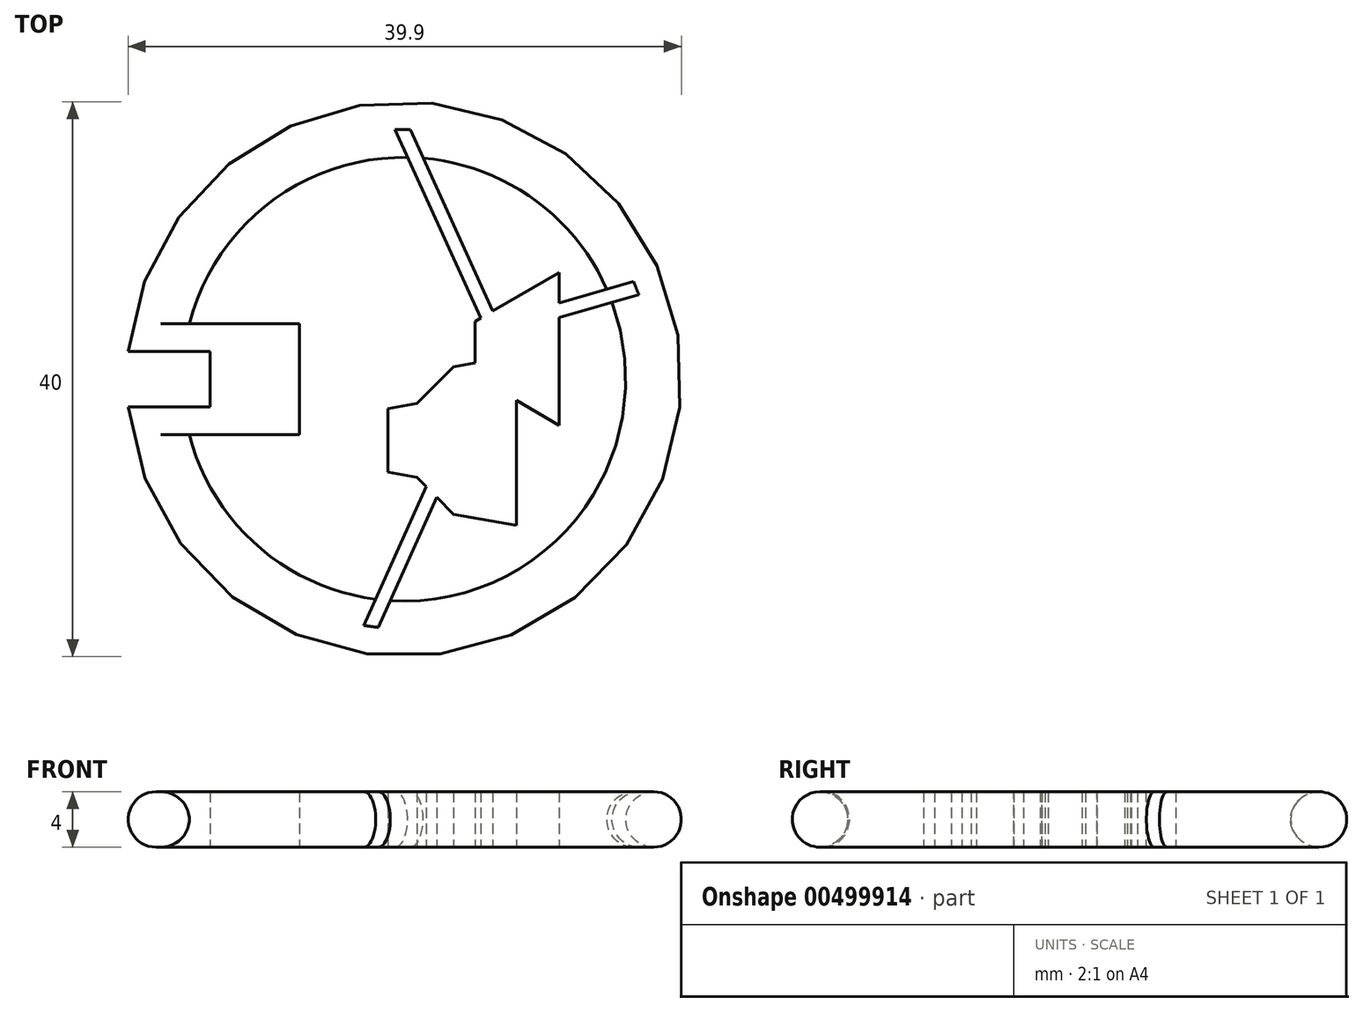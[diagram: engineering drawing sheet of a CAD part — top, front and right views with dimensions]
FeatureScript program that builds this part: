
annotation { "Feature Type Name" : "Feature", "Feature Type Description" : "" }
export const myFeature = defineFeature(function(context is Context, id is Id, definition is map)
    precondition{}
    {
        {
            var Q0;
            Q0=qCreatedBy(makeId("Front.planeOp"),FACE);
            var sketch = newSketch(context, id + "F0", { "sketchPlane" : qUnion([Q0])});
            skCircle(sketch, "E0", {"center": v(0, 0) * mm, "radius": 2 * mm});
            skLineSegment(sketch, "E1", {"start": v(18, -10.27) * mm, "end": v(18, 20.7) * mm});
            skPoint(sketch, "E2.start.orphan", {"position": v(-2, 0) * mm});
            skSolve(sketch);
        }
        {
            var Q0;
            Q0=makeQuery(id+"F0.imprint","IMPRINT",FACE,{"disambiguationData":[TD([[makeQuery(id+"F0.imprint","IMPRINT",EDGE,{"derivedFrom":sQuery(id+"F0.wireOp",EDGE,"E0")}),1.0]])]});
            var Q1;
            Q1=sQuery(id+"F0.wireOp",EDGE,"E1");
            revolve(context, id + "F1", {"entities" : qUnion([Q0]), "axis" : qUnion([Q1]), "revolveType" : RevolveType.FULL});
        }
        {
            var Q0;
            Q0=qCreatedBy(makeId("Top.planeOp"),FACE);
            var sketch = newSketch(context, id + "F2", { "sketchPlane" : qUnion([Q0])});
            skLineSegment(sketch, "E3.bottom", {"start": v(4, 4) * mm, "end": v(10.45, 4) * mm});
            skLineSegment(sketch, "E3.right", {"start": v(10.45, 4) * mm, "end": v(10.45, -4) * mm});
            skArc(sketch, "E4", {"start": v(-1.6, 4) * mm, "mid": v(-2, 0) * mm, "end": v(-1.6, -4) * mm});
            skArc(sketch, "E5.0", {"start": v(0.36, 3.6) * mm, "mid": v(0, 0) * mm, "end": v(0.36, -3.6) * mm});
            skLineSegment(sketch, "E6", {"start": v(4, 4) * mm, "end": v(0.45, 4) * mm});
            skLineSegment(sketch, "E7", {"start": v(10.45, -4) * mm, "end": v(0.45, -4) * mm});
            skLineSegment(sketch, "E8", {"start": v(0.36, 3.6) * mm, "end": v(0.45, 4) * mm});
            skLineSegment(sketch, "E9", {"start": v(0.36, -3.6) * mm, "end": v(0.45, -4) * mm});
            skSolve(sketch);
        }
        {
            var Q0;
            Q0 = qSketchRegion(id + "F2", true);
            extrude(context, id + "F3", {"entities" : qUnion([Q0]), "operationType" : NewBodyOperationType.ADD, "endBound" : BoundingType.SYMMETRIC, "depth" : 4 * mm});
        }
        {
            var Q0;
            Q0=qCreatedBy(makeId("Right.planeOp"),FACE);
            var sketch = newSketch(context, id + "F4", { "sketchPlane" : qUnion([Q0])});
            skLineSegment(sketch, "E10", {"start": v(2, 2) * mm, "end": v(-2, 2) * mm});
            skLineSegment(sketch, "E11.top", {"start": v(2, -2) * mm, "end": v(-2, -2) * mm});
            skLineSegment(sketch, "E11.left", {"start": v(2, 2) * mm, "end": v(2, -2) * mm});
            skLineSegment(sketch, "E11.right", {"start": v(-2, 2) * mm, "end": v(-2, -2) * mm});
            skLineSegment(sketch, "E12.0.0", {"start": v(-2, -2) * mm, "end": v(2, -2) * mm});
            skPoint(sketch, "E13.0.end.orphan", {"position": v(4, -2) * mm});
            skPoint(sketch, "E14.orphan", {"position": v(4, 2) * mm});
            skSolve(sketch);
        }
        {
            var Q0;
            Q0 = qSketchRegion(id + "F4", true);
            extrude(context, id + "F5", {"entities" : qUnion([Q0]), "operationType" : NewBodyOperationType.REMOVE, "endBound" : BoundingType.SYMMETRIC, "depth" : 8 * mm});
        }
        {
            var Q0;
            Q0=makeQuery(id+"F3.opExtrude","CAP_FACE",FACE,{"disambiguationData":[OSD([sQuery(id+"F2.wireOp",EDGE,"E3.bottom"),sQuery(id+"F2.wireOp",EDGE,"E3.top"),sQuery(id+"F2.wireOp",EDGE,"E3.right"),sQuery(id+"F2.wireOp",EDGE,"E5.0"),sQuery(id+"F2.wireOp",EDGE,"BC0NbM3x-ihGr-PsGI-ILSp-vhnntA4KJWQ9"),sQuery(id+"F2.wireOp",EDGE,"AOes4hMv-feAn-fqFm-8PAN-h10fPkBZOwOo")])],"isStart":true});
            var sketch = newSketch(context, id + "F6", { "sketchPlane" : qUnion([Q0])});
            skLineSegment(sketch, "E15.0", {"start": v(4, -2) * mm, "end": v(4, 2) * mm});
            skLineSegment(sketch, "E16.0", {"start": v(10.45, -4) * mm, "end": v(10.45, -4) * mm});
            skLineSegment(sketch, "E17", {"start": v(26.1, 10.53) * mm, "end": v(26.1, 1.53) * mm});
            skLineSegment(sketch, "E18", {"start": v(26.1, 1.53) * mm, "end": v(29.2, 3.33) * mm});
            skLineSegment(sketch, "E19", {"start": v(29.2, 3.33) * mm, "end": v(29.2, -7.67) * mm});
            skLineSegment(sketch, "E20", {"start": v(29.2, -7.67) * mm, "end": v(23.14, -4.17) * mm});
            skLineSegment(sketch, "E21", {"start": v(26.1, 1.53) * mm, "end": v(23.14, -0.17) * mm});
            skLineSegment(sketch, "E22", {"start": v(23.14, -0.17) * mm, "end": v(23.14, -4.17) * mm});
            skLineSegment(sketch, "E23", {"start": v(26.1, 10.53) * mm, "end": v(21.58, 9.74) * mm});
            skLineSegment(sketch, "E24", {"start": v(21.58, 9.74) * mm, "end": v(18.92, 7.08) * mm});
            skLineSegment(sketch, "E25", {"start": v(18.92, 7.08) * mm, "end": v(16.82, 6.71) * mm});
            skLineSegment(sketch, "E26", {"start": v(16.82, 6.71) * mm, "end": v(16.82, 2.12) * mm});
            skLineSegment(sketch, "E27", {"start": v(16.82, 2.12) * mm, "end": v(18.92, 1.75) * mm});
            skLineSegment(sketch, "E28", {"start": v(18.92, 1.75) * mm, "end": v(21.58, -0.9) * mm});
            skLineSegment(sketch, "E29", {"start": v(21.58, -0.9) * mm, "end": v(23.14, -1.17) * mm});
            skPoint(sketch, "E30.end.orphan", {"position": v(26.1, -1.7) * mm});
            skLineSegment(sketch, "E31", {"start": v(26.1, 1.53) * mm, "end": v(26.1, -1.7) * mm});
            skLineSegment(sketch, "E32", {"start": v(23.14, -1.17) * mm, "end": v(26.1, -1.7) * mm});
            skArc(sketch, "E33", {"start": v(-1.9, -2) * mm, "mid": v(38, 0) * mm, "end": v(-1.9, 2) * mm});
            skArc(sketch, "E34", {"start": v(2.5, -4) * mm, "mid": v(8.3, -12.73) * mm, "end": v(18.26, -16) * mm});
            skArc(sketch, "E35.0", {"start": v(0.57, -4.5) * mm, "mid": v(16.66, -17.95) * mm, "end": v(34.57, -7.04) * mm, "construction": true});
            skLineSegment(sketch, "E36", {"start": v(30.73, 12.72) * mm, "end": v(26.1, 9.23) * mm});
            skLineSegment(sketch, "E37", {"start": v(26.1, 9.23) * mm, "end": v(26.1, 7.98) * mm});
            skLineSegment(sketch, "E38", {"start": v(26.1, 7.98) * mm, "end": v(31.42, 12) * mm});
            skLineSegment(sketch, "E39", {"start": v(29.2, -4.45) * mm, "end": v(34.93, -6.1) * mm});
            skLineSegment(sketch, "E40", {"start": v(34.93, -6.1) * mm, "end": v(29.2, -4.45) * mm});
            skLineSegment(sketch, "E41", {"start": v(29.2, -5.5) * mm, "end": v(34.57, -7.04) * mm});
            skLineSegment(sketch, "E42", {"start": v(23.53, -4.4) * mm, "end": v(17.35, -17.99) * mm});
            skLineSegment(sketch, "E43", {"start": v(17.35, -17.99) * mm, "end": v(23.53, -4.4) * mm});
            skLineSegment(sketch, "E44", {"start": v(24.4, -4.9) * mm, "end": v(18.45, -18) * mm});
            skLineSegment(sketch, "E45", {"start": v(19.6, 7.75) * mm, "end": v(15.1, 17.76) * mm});
            skLineSegment(sketch, "E46", {"start": v(15.1, 17.76) * mm, "end": v(19.6, 7.75) * mm});
            skLineSegment(sketch, "E47", {"start": v(20.35, 8.51) * mm, "end": v(16.13, 17.9) * mm});
            skArc(sketch, "E48.trimOffspring", {"start": v(29.12, 11.5) * mm, "mid": v(23.53, 15.01) * mm, "end": v(17, 15.97) * mm});
            skArc(sketch, "E49.trimOffspring", {"start": v(33, -5.55) * mm, "mid": v(33.7, 3.06) * mm, "end": v(29.82, 10.79) * mm});
            skArc(sketch, "E50.trimOffspring", {"start": v(34.93, -6.1) * mm, "mid": v(23.3, 17.2) * mm, "end": v(0.57, 4.5) * mm, "construction": true});
            skLineSegment(sketch, "E51", {"start": v(34.93, -6.1) * mm, "end": v(34.57, -7.04) * mm});
            skLineSegment(sketch, "E52", {"start": v(30.73, 12.72) * mm, "end": v(31.42, 12) * mm});
            skLineSegment(sketch, "E53", {"start": v(15.1, 17.76) * mm, "end": v(16.13, 17.9) * mm});
            skArc(sketch, "E54.trimOffspring", {"start": v(15.95, 15.87) * mm, "mid": v(7.41, 12) * mm, "end": v(2.5, 4) * mm});
            skArc(sketch, "E55.trimOffspring", {"start": v(19.38, -15.94) * mm, "mid": v(27.3, -13.02) * mm, "end": v(32.63, -6.48) * mm});
            skLineSegment(sketch, "E56", {"start": v(18.45, -18) * mm, "end": v(17.35, -17.99) * mm});
            skSolve(sketch);
        }
        {
            var Q0;
            {var subQ5=sQuery(id+"F6.wireOp",EDGE,"E37");Q0=makeQuery(id+"F6.imprint","IMPRINT",FACE,{"disambiguationData":[TD([[makeQuery(id+"F6.imprint","IMPRINT",EDGE,{"derivedFrom":subQ5}),1.0]])]});}
            var Q1;
            {var subQ4=sQuery(id+"F6.wireOp",EDGE,"E53");Q1=makeQuery(id+"F6.imprint","IMPRINT",FACE,{"disambiguationData":[TD([[makeQuery(id+"F6.imprint","IMPRINT",EDGE,{"derivedFrom":subQ4}),-1.0]])]});}
            var Q2;
            {var subQ8=sQuery(id+"F6.wireOp",EDGE,"E21");Q2=makeQuery(id+"F6.imprint","IMPRINT",FACE,{"disambiguationData":[TD([[makeQuery(id+"F6.imprint","IMPRINT",EDGE,{"derivedFrom":subQ8}),-1.0]])]});}
            var Q3;
            {var subQ5=sQuery(id+"F6.wireOp",EDGE,"E18");Q3=makeQuery(id+"F6.imprint","IMPRINT",FACE,{"disambiguationData":[TD([[makeQuery(id+"F6.imprint","IMPRINT",EDGE,{"derivedFrom":subQ5}),-1.0]])]});}
            var Q4;
            {var subQ0=sQuery(id+"F6.wireOp",EDGE,"E21");Q4=makeQuery(id+"F6.imprint","IMPRINT",FACE,{"disambiguationData":[TD([[makeQuery(id+"F6.imprint","IMPRINT",EDGE,{"derivedFrom":subQ0}),1.0]])]});}
            var Q5;
            {var subQ7=sQuery(id+"F6.wireOp",EDGE,"E51");Q5=makeQuery(id+"F6.imprint","IMPRINT",FACE,{"disambiguationData":[TD([[makeQuery(id+"F6.imprint","IMPRINT",EDGE,{"derivedFrom":subQ7}),-1.0]])]});}
            var Q6;
            {var subQ7=sQuery(id+"F6.wireOp",EDGE,"E56");Q6=makeQuery(id+"F6.imprint","IMPRINT",FACE,{"disambiguationData":[TD([[makeQuery(id+"F6.imprint","IMPRINT",EDGE,{"derivedFrom":subQ7}),-1.0]])]});}
            extrude(context, id + "F7", {"entities" : qUnion([Q0, Q1, Q2, Q3, Q4, Q5, Q6]), "operationType" : NewBodyOperationType.ADD, "oppositeDirection" : true, "depth" : 4 * mm});
        }
    });
